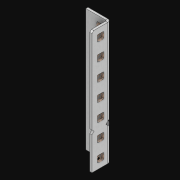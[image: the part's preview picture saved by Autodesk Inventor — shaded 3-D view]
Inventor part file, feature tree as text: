
AUTODESK INVENTOR PART (.ipt)
format: ipt  version: 2021 (Build 250183000, 183)  size: 1,080,320 bytes
history: native  units: in
note: dims shown in document units (in); Inventor stores cm internally (conversion verified against a paired STEP export)
features: extrude x16, other x14, sketch x4, pattern_linear x2, sheet_metal_op x1
ambient origin geometry x8: Origin, YZ Plane, XZ Plane, XY Plane, X Axis, Y Axis, Z Axis, Center Point
bodies: Solid1 (feature_tree)
feature tree (37):
  pattern_linear  "Rectangular Pattern1"  Spacing1=0.5in  [1 undecoded]
  pattern_linear  "Rectangular Pattern3"  Count1=7  [1 undecoded]
  extrude  "Extrusion1"  Depth=0.5in
  extrude  "Extrusion2"  Depth=0.5in
  sketch  "Sketch1"  dims[d0=0.182in]
  other  "Srf1"
  sketch  "Sketch3"  dims[d1=0.063in d2=0.0in]
  other  "Srf3"
  other  "Srf4"
  other  "Srf5"
  other  "Srf6"
  other  "Srf7"
  other  "Srf8"
  other  "Srf9"
  other  "Srf142"
  other  "Srf143"
  other  "Srf144"
  other  "Srf145"
  other  "Srf146"
  other  "Srf147"
  sketch  "Sketch4"  dims[d6=0.182in]
  sketch  "Sketch5"  dims[d7=0.063in d8=0.0in d11=0.5in d12=0.3937in d14=0.5in d18=2.7559in d20=0.5in d21=14.0in d22=0.0in d23=0.841in d24=0.0in]
  sheet_metal_op  "Fold1"
  extrude  "ExtrusionSrf1"  TaperAngle=0.0deg  [1 undecoded]
  extrude  "ExtrusionSrf3"  Depth=0.5in TaperAngle=0.0deg
  extrude  "ExtrusionSrf4"  [1 undecoded]
  extrude  "ExtrusionSrf5"  [1 undecoded]
  extrude  "ExtrusionSrf6"  [1 undecoded]
  extrude  "ExtrusionSrf7"  [1 undecoded]
  extrude  "ExtrusionSrf8"  [1 undecoded]
  extrude  "ExtrusionSrf9"  [1 undecoded]
  extrude  "ExtrusionSrf142"  [1 undecoded]
  extrude  "ExtrusionSrf143"  [1 undecoded]
  extrude  "ExtrusionSrf144"  [1 undecoded]
  extrude  "ExtrusionSrf145"  [1 undecoded]
  extrude  "ExtrusionSrf146"  [1 undecoded]
  extrude  "ExtrusionSrf147"  [1 undecoded]
note: 15 required parameter values undecoded (feature->parameter linkage not recoverable at this tier; creation-order binding heuristic only, values carry confidence <= 0.55)
